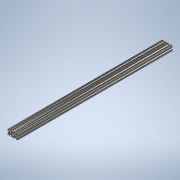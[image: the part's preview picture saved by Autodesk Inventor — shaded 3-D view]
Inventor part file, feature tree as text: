
AUTODESK INVENTOR PART (.ipt)
format: ipt  version: 2020 (Build 240168000, 168)  size: 357,888 bytes
history: native  units: in
note: dims shown in document units (in); Inventor stores cm internally (conversion verified against a paired STEP export)
features: sketch x2, extrude x1
ambient origin geometry x8: Origin, YZ Plane, XZ Plane, XY Plane, X Axis, Y Axis, Z Axis, Center Point
bodies: Solid1 (feature_tree)
feature tree (3):
  extrude  "Extrusion1"  [1 undecoded]
  sketch  "Sketch2"
  sketch  "Sketch1"  dims[d0=30.0in d1=0.0in]
note: 1 required parameter value undecoded (feature->parameter linkage not recoverable at this tier; creation-order binding heuristic only, values carry confidence <= 0.55)
